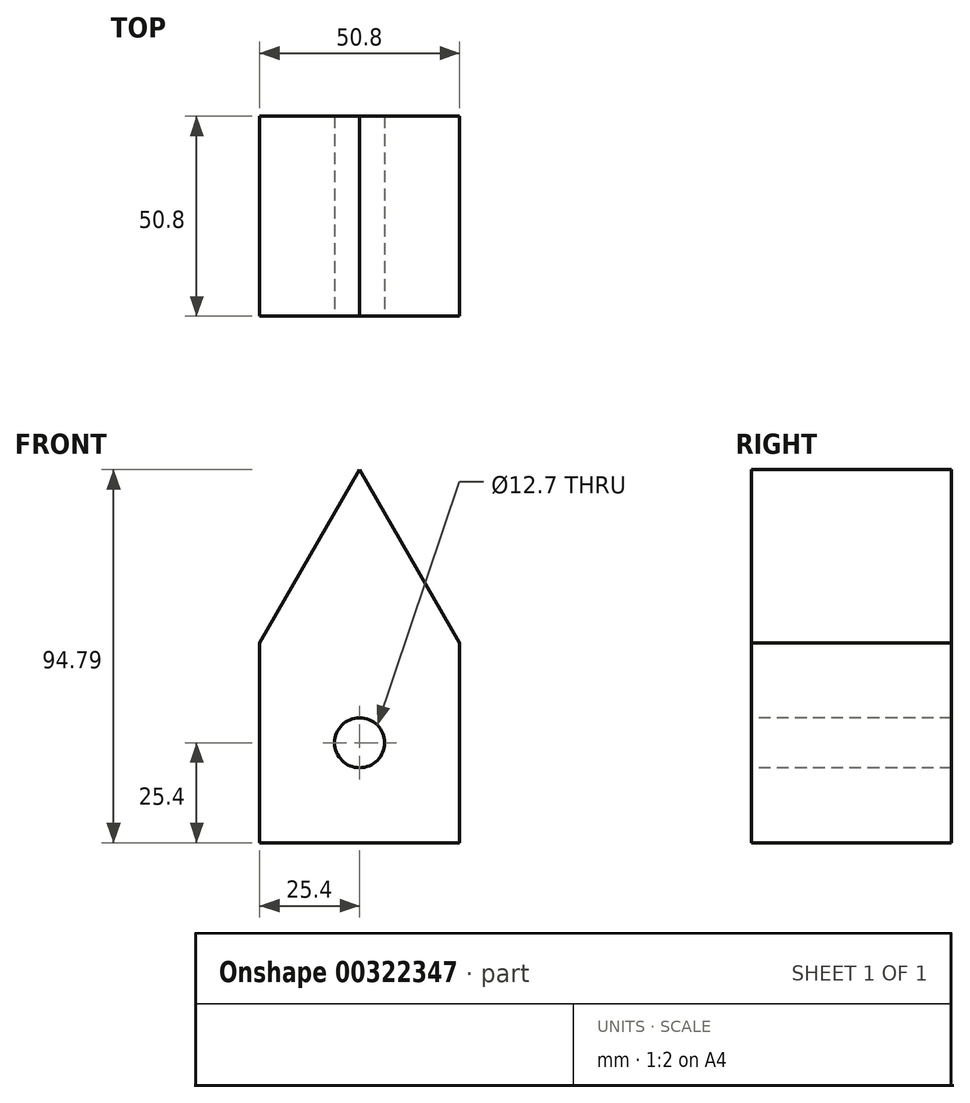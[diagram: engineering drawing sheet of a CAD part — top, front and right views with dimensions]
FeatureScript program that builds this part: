
annotation { "Feature Type Name" : "Feature", "Feature Type Description" : "" }
export const myFeature = defineFeature(function(context is Context, id is Id, definition is map)
    precondition{}
    {
        {
            var Q0;
            Q0=qCreatedBy(makeId("Front.planeOp"),FACE);
            var sketch = newSketch(context, id + "F0", { "sketchPlane" : qUnion([Q0])});
            skLineSegment(sketch, "E0.bottom", {"start": v(25.4, -25.4) * mm, "end": v(-25.4, -25.4) * mm});
            skLineSegment(sketch, "E0.left", {"start": v(25.4, -25.4) * mm, "end": v(25.4, 25.4) * mm});
            skLineSegment(sketch, "E0.right", {"start": v(-25.4, -25.4) * mm, "end": v(-25.4, 25.4) * mm});
            skPoint(sketch, "E0.middle", {"position": v(0, 0) * mm});
            skLineSegment(sketch, "E1", {"start": v(-25.4, 25.4) * mm, "end": v(0, 69.4) * mm});
            skLineSegment(sketch, "E2", {"start": v(25.4, 25.4) * mm, "end": v(0, 69.4) * mm});
            skCircle(sketch, "E3", {"center": v(0, 0) * mm, "radius": 6.35 * mm});
            skSolve(sketch);
        }
        {
            var Q0;
            Q0=makeQuery(id+"F0.imprint","IMPRINT",FACE,{"disambiguationData":[TD([[makeQuery(id+"F0.imprint","IMPRINT",EDGE,{"derivedFrom":sQuery(id+"F0.wireOp",EDGE,"E0.bottom")}),-1.0]])]});
            extrude(context, id + "F1", {"entities" : qUnion([Q0]), "oppositeDirection" : true, "depth" : 50.8 * mm});
        }
    });
